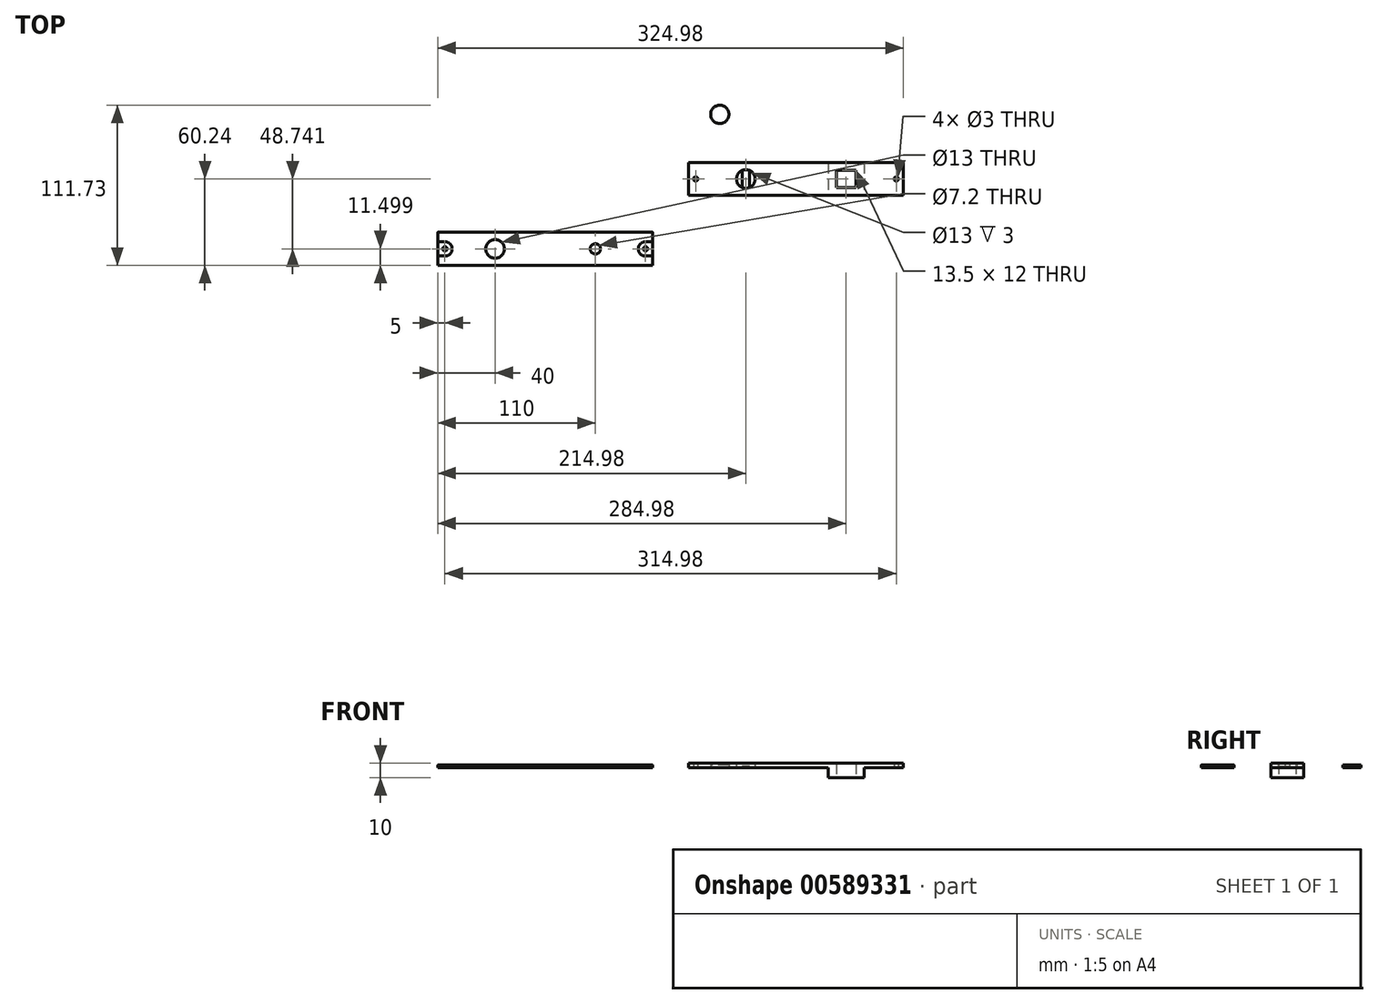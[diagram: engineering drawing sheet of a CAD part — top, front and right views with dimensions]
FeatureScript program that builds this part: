
annotation { "Feature Type Name" : "Feature", "Feature Type Description" : "" }
export const myFeature = defineFeature(function(context is Context, id is Id, definition is map)
    precondition{}
    {
        {
            var Q0;
            Q0=qCreatedBy(makeId("Top.planeOp"),FACE);
            var sketch = newSketch(context, id + "F0", { "sketchPlane" : qUnion([Q0])});
            skLineSegment(sketch, "E0.bottom", {"start": v(75, -11.5) * mm, "end": v(-75, -11.5) * mm});
            skLineSegment(sketch, "E0.top", {"start": v(75, 11.5) * mm, "end": v(-75, 11.5) * mm});
            skLineSegment(sketch, "E0.left", {"start": v(75, -11.5) * mm, "end": v(75, 11.5) * mm});
            skLineSegment(sketch, "E0.right", {"start": v(-75, -11.5) * mm, "end": v(-75, 11.5) * mm});
            skPoint(sketch, "E0.middle", {"position": v(0, 0) * mm});
            skCircle(sketch, "E1", {"center": v(-35, 0) * mm, "radius": 6.5 * mm});
            skLineSegment(sketch, "E2.bottom", {"start": v(-75, 11.5) * mm, "end": v(-65, 11.5) * mm, "construction": true});
            skLineSegment(sketch, "E2.top", {"start": v(-75, -11.5) * mm, "end": v(-65, -11.5) * mm, "construction": true});
            skLineSegment(sketch, "E2.left", {"start": v(-75, 11.5) * mm, "end": v(-75, -11.5) * mm, "construction": true});
            skLineSegment(sketch, "E2.right", {"start": v(-65, 11.5) * mm, "end": v(-65, -11.5) * mm, "construction": true});
            skLineSegment(sketch, "E3.bottom", {"start": v(75, -11.5) * mm, "end": v(65, -11.5) * mm, "construction": true});
            skLineSegment(sketch, "E3.top", {"start": v(75, 11.5) * mm, "end": v(65, 11.5) * mm, "construction": true});
            skLineSegment(sketch, "E3.left", {"start": v(75, -11.5) * mm, "end": v(75, 11.5) * mm, "construction": true});
            skLineSegment(sketch, "E3.right", {"start": v(65, -11.5) * mm, "end": v(65, 11.5) * mm, "construction": true});
            skLineSegment(sketch, "E4.bottom", {"start": v(41.75, -6) * mm, "end": v(28.25, -6) * mm});
            skLineSegment(sketch, "E4.top", {"start": v(41.75, 6) * mm, "end": v(28.25, 6) * mm});
            skLineSegment(sketch, "E4.left", {"start": v(41.75, -6) * mm, "end": v(41.75, 6) * mm});
            skLineSegment(sketch, "E4.right", {"start": v(28.25, -6) * mm, "end": v(28.25, 6) * mm});
            skPoint(sketch, "E4.middle", {"position": v(35, 0) * mm});
            skLineSegment(sketch, "E5.bottom", {"start": v(39, -6) * mm, "end": v(31, -6) * mm});
            skLineSegment(sketch, "E5.top", {"start": v(39, 6) * mm, "end": v(31, 6) * mm});
            skLineSegment(sketch, "E5.left", {"start": v(39, -6) * mm, "end": v(39, 6) * mm});
            skLineSegment(sketch, "E5.right", {"start": v(31, -6) * mm, "end": v(31, 6) * mm});
            skCircle(sketch, "E6", {"center": v(-70, 0) * mm, "radius": 1.5 * mm});
            skLineSegment(sketch, "E7.bottom", {"start": v(-65, 11.5) * mm, "end": v(-67, 11.5) * mm, "construction": true});
            skLineSegment(sketch, "E7.top", {"start": v(-65, -11.5) * mm, "end": v(-67, -11.5) * mm, "construction": true});
            skLineSegment(sketch, "E7.right", {"start": v(-67, 11.5) * mm, "end": v(-67, -11.5) * mm, "construction": true});
            skCircle(sketch, "E8", {"center": v(70, 0) * mm, "radius": 1.5 * mm});
            skLineSegment(sketch, "E9.bottom", {"start": v(-32.5, -6) * mm, "end": v(-37.5, -6) * mm, "construction": true});
            skLineSegment(sketch, "E9.top", {"start": v(-32.5, 6) * mm, "end": v(-37.5, 6) * mm, "construction": true});
            skLineSegment(sketch, "E9.left", {"start": v(-32.5, -6) * mm, "end": v(-32.5, 6) * mm});
            skLineSegment(sketch, "E9.right", {"start": v(-37.5, -6) * mm, "end": v(-37.5, 6) * mm});
            skSolve(sketch);
        }
        {
            var Q0;
            Q0=makeQuery(id+"F0.imprint","IMPRINT",FACE,{"disambiguationData":[TD([[makeQuery(id+"F0.imprint","IMPRINT",EDGE,{"derivedFrom":sQuery(id+"F0.wireOp",EDGE,"E0.bottom")}),-1.0]])]});
            var Q1;
            Q1=makeQuery(id+"F0.imprint","IMPRINT",FACE,{"disambiguationData":[TD([[makeQuery(id+"F0.imprint","IMPRINT",EDGE,{"derivedFrom":sQuery(id+"F0.wireOp",EDGE,"E5.bottom")}),-1.0]])]});
            var Q2;
            {var subQ0=sQuery(id+"F0.wireOp",EDGE,"E9.left");Q2=makeQuery(id+"F0.imprint","IMPRINT",FACE,{"disambiguationData":[TD([[makeQuery(id+"F0.imprint","IMPRINT",EDGE,{"derivedFrom":subQ0}),1.0]])]});}
            extrude(context, id + "F1", {"entities" : qUnion([Q0, Q1, Q2]), "depth" : 3 * mm});
        }
        {
            var Q0;
            Q0=qCreatedBy(makeId("Top.planeOp"),FACE);
            var sketch = newSketch(context, id + "F2", { "sketchPlane" : qUnion([Q0])});
            skLineSegment(sketch, "E10.bottom", {"start": v(-99.98, -60.24) * mm, "end": v(-249.98, -60.24) * mm});
            skLineSegment(sketch, "E10.top", {"start": v(-99.98, -37.24) * mm, "end": v(-249.98, -37.24) * mm});
            skLineSegment(sketch, "E10.left", {"start": v(-99.98, -60.24) * mm, "end": v(-99.98, -37.24) * mm});
            skLineSegment(sketch, "E10.right", {"start": v(-249.98, -60.24) * mm, "end": v(-249.98, -37.24) * mm});
            skPoint(sketch, "E10.middle", {"position": v(-174.98, -48.74) * mm});
            skCircle(sketch, "E11", {"center": v(-209.98, -48.74) * mm, "radius": 6.5 * mm});
            skLineSegment(sketch, "E12.bottom", {"start": v(-249.98, -37.24) * mm, "end": v(-239.98, -37.24) * mm, "construction": true});
            skLineSegment(sketch, "E12.top", {"start": v(-249.98, -60.24) * mm, "end": v(-239.98, -60.24) * mm, "construction": true});
            skLineSegment(sketch, "E12.left", {"start": v(-249.98, -37.24) * mm, "end": v(-249.98, -60.24) * mm, "construction": true});
            skLineSegment(sketch, "E12.right", {"start": v(-239.98, -37.24) * mm, "end": v(-239.98, -60.24) * mm, "construction": true});
            skLineSegment(sketch, "E13.bottom", {"start": v(-99.98, -60.24) * mm, "end": v(-109.98, -60.24) * mm, "construction": true});
            skLineSegment(sketch, "E13.top", {"start": v(-99.98, -37.24) * mm, "end": v(-109.98, -37.24) * mm, "construction": true});
            skLineSegment(sketch, "E13.left", {"start": v(-99.98, -60.24) * mm, "end": v(-99.98, -37.24) * mm, "construction": true});
            skLineSegment(sketch, "E13.right", {"start": v(-109.98, -60.24) * mm, "end": v(-109.98, -37.24) * mm, "construction": true});
            skLineSegment(sketch, "E14.bottom", {"start": v(-131.98, -55.74) * mm, "end": v(-147.98, -55.74) * mm, "construction": true});
            skLineSegment(sketch, "E14.top", {"start": v(-131.98, -41.74) * mm, "end": v(-147.98, -41.74) * mm, "construction": true});
            skLineSegment(sketch, "E14.left", {"start": v(-131.98, -55.74) * mm, "end": v(-131.98, -41.74) * mm, "construction": true});
            skLineSegment(sketch, "E14.right", {"start": v(-147.98, -55.74) * mm, "end": v(-147.98, -41.74) * mm, "construction": true});
            skPoint(sketch, "E14.middle", {"position": v(-139.98, -48.74) * mm});
            skLineSegment(sketch, "E15.bottom", {"start": v(-135.98, -55.74) * mm, "end": v(-143.98, -55.74) * mm});
            skLineSegment(sketch, "E15.top", {"start": v(-135.98, -41.74) * mm, "end": v(-143.98, -41.74) * mm});
            skLineSegment(sketch, "E15.left", {"start": v(-135.98, -55.74) * mm, "end": v(-135.98, -41.74) * mm, "construction": true});
            skLineSegment(sketch, "E15.right", {"start": v(-143.98, -55.74) * mm, "end": v(-143.98, -41.74) * mm, "construction": true});
            skCircle(sketch, "E16", {"center": v(-244.98, -48.74) * mm, "radius": 1.5 * mm});
            skCircle(sketch, "E17", {"center": v(-244.98, -55.24) * mm, "radius": 1.5 * mm, "construction": true});
            skCircle(sketch, "E18", {"center": v(-104.98, -48.74) * mm, "radius": 1.5 * mm});
            skCircle(sketch, "E19", {"center": v(-104.98, -55.24) * mm, "radius": 1.5 * mm, "construction": true});
            skCircle(sketch, "E20", {"center": v(-139.98, -48.74) * mm, "radius": 3.6 * mm});
            skLineSegment(sketch, "E21.bottom", {"start": v(-207.48, -54.74) * mm, "end": v(-212.48, -54.74) * mm, "construction": true});
            skLineSegment(sketch, "E21.top", {"start": v(-207.48, -42.74) * mm, "end": v(-212.48, -42.74) * mm, "construction": true});
            skLineSegment(sketch, "E21.left", {"start": v(-207.48, -54.74) * mm, "end": v(-207.48, -42.74) * mm});
            skLineSegment(sketch, "E21.right", {"start": v(-212.48, -54.74) * mm, "end": v(-212.48, -42.74) * mm});
            skSolve(sketch);
        }
        {
            var Q0;
            Q0=makeQuery(id+"F2.imprint","IMPRINT",FACE,{"disambiguationData":[TD([[makeQuery(id+"F2.imprint","IMPRINT",EDGE,{"derivedFrom":sQuery(id+"F2.wireOp",EDGE,"E10.bottom")}),-1.0]])]});
            extrude(context, id + "F3", {"entities" : qUnion([Q0]), "depth" : 2 * mm});
        }
        {
            var Q0;
            Q0=makeQuery(id+"F1.opExtrude","CAP_FACE",FACE,{"disambiguationData":[OSD([sQuery(id+"F0.wireOp",EDGE,"E0.bottom"),sQuery(id+"F0.wireOp",EDGE,"E0.top"),sQuery(id+"F0.wireOp",EDGE,"E0.left"),sQuery(id+"F0.wireOp",EDGE,"E0.right"),sQuery(id+"F0.wireOp",EDGE,"E1"),sQuery(id+"F0.wireOp",EDGE,"E4.bottom"),sQuery(id+"F0.wireOp",EDGE,"E4.top"),sQuery(id+"F0.wireOp",EDGE,"E4.left"),sQuery(id+"F0.wireOp",EDGE,"E4.right"),sQuery(id+"F0.wireOp",EDGE,"E5.left"),sQuery(id+"F0.wireOp",EDGE,"E5.right")])],"isStart":true});
            var sketch = newSketch(context, id + "F4", { "sketchPlane" : qUnion([Q0])});
            skPoint(sketch, "E22.0", {"position": v(35, 0) * mm});
            skLineSegment(sketch, "E23.bottom", {"start": v(47.5, -11.5) * mm, "end": v(22.5, -11.5) * mm});
            skLineSegment(sketch, "E23.top", {"start": v(47.5, 11.5) * mm, "end": v(22.5, 11.5) * mm});
            skLineSegment(sketch, "E23.left", {"start": v(47.5, -11.5) * mm, "end": v(47.5, 11.5) * mm});
            skLineSegment(sketch, "E23.right", {"start": v(22.5, -11.5) * mm, "end": v(22.5, 11.5) * mm});
            skLineSegment(sketch, "E24.bottom", {"start": v(41.75, -6) * mm, "end": v(28.25, -6) * mm});
            skLineSegment(sketch, "E24.top", {"start": v(41.75, 6) * mm, "end": v(28.25, 6) * mm});
            skLineSegment(sketch, "E24.left", {"start": v(41.75, -6) * mm, "end": v(41.75, 6) * mm});
            skLineSegment(sketch, "E24.right", {"start": v(28.25, -6) * mm, "end": v(28.25, 6) * mm});
            skLineSegment(sketch, "E25.bottom", {"start": v(39, -6) * mm, "end": v(31, -6) * mm});
            skLineSegment(sketch, "E25.top", {"start": v(39, 6) * mm, "end": v(31, 6) * mm});
            skLineSegment(sketch, "E25.left", {"start": v(39, -6) * mm, "end": v(39, 6) * mm});
            skLineSegment(sketch, "E25.right", {"start": v(31, -6) * mm, "end": v(31, 6) * mm});
            skSolve(sketch);
        }
        {
            var Q0;
            Q0=qSketchRegion(id+"F4",true);
            var Q1;
            Q1=makeQuery(id+"F0.imprint","IMPRINT",FACE,{"disambiguationData":[TD([[makeQuery(id+"F0.imprint","IMPRINT",EDGE,{"derivedFrom":sQuery(id+"F0.wireOp",EDGE,"E5.bottom")}),-1.0]])]});
            extrude(context, id + "F5", {"entities" : qUnion([Q0, Q1]), "operationType" : NewBodyOperationType.ADD, "depth" : 7 * mm});
        }
        {
            var Q0;
            Q0=makeQuery(id+"F1.opExtrude","CAP_FACE",FACE,{"disambiguationData":[OSD([sQuery(id+"F0.wireOp",EDGE,"E0.bottom"),sQuery(id+"F0.wireOp",EDGE,"E0.top"),sQuery(id+"F0.wireOp",EDGE,"E0.left"),sQuery(id+"F0.wireOp",EDGE,"E0.right"),sQuery(id+"F0.wireOp",EDGE,"E1"),sQuery(id+"F0.wireOp",EDGE,"E4.bottom"),sQuery(id+"F0.wireOp",EDGE,"E4.top"),sQuery(id+"F0.wireOp",EDGE,"E4.left"),sQuery(id+"F0.wireOp",EDGE,"E4.right"),sQuery(id+"F0.wireOp",EDGE,"E5.left"),sQuery(id+"F0.wireOp",EDGE,"E5.right")])],"isStart":false});
            var sketch = newSketch(context, id + "F6", { "sketchPlane" : qUnion([Q0])});
            skPoint(sketch, "E26.0", {"position": v(35, 0) * mm});
            skLineSegment(sketch, "E27.bottom", {"start": v(41.75, -6) * mm, "end": v(28.25, -6) * mm});
            skLineSegment(sketch, "E27.top", {"start": v(41.75, 6) * mm, "end": v(28.25, 6) * mm});
            skLineSegment(sketch, "E27.left", {"start": v(41.75, -6) * mm, "end": v(41.75, 6) * mm});
            skLineSegment(sketch, "E27.right", {"start": v(28.25, -6) * mm, "end": v(28.25, 6) * mm});
            skSolve(sketch);
        }
        {
            var Q0;
            Q0=qSketchRegion(id+"F6",true);
            extrude(context, id + "F7", {"entities" : qUnion([Q0]), "operationType" : NewBodyOperationType.REMOVE, "oppositeDirection" : true, "depth" : 9 * mm});
        }
        {
            var Q0;
            Q0=makeQuery(id+"F1.opExtrude","CAP_FACE",FACE,{"disambiguationData":[OSD([sQuery(id+"F0.wireOp",EDGE,"E0.bottom"),sQuery(id+"F0.wireOp",EDGE,"E0.top"),sQuery(id+"F0.wireOp",EDGE,"E0.left"),sQuery(id+"F0.wireOp",EDGE,"E0.right"),sQuery(id+"F0.wireOp",EDGE,"E1"),sQuery(id+"F0.wireOp",EDGE,"E4.bottom"),sQuery(id+"F0.wireOp",EDGE,"E4.top"),sQuery(id+"F0.wireOp",EDGE,"E4.left"),sQuery(id+"F0.wireOp",EDGE,"E4.right"),sQuery(id+"F0.wireOp",EDGE,"E5.left"),sQuery(id+"F0.wireOp",EDGE,"E5.right"),sQuery(id+"F0.wireOp",EDGE,"E6"),sQuery(id+"F0.wireOp",EDGE,"uwKOgWHx-wiQu-w8Me-ZzSO-K48oh4q2hqjQ"),sQuery(id+"F0.wireOp",EDGE,"E8"),sQuery(id+"F0.wireOp",EDGE,"GEiIiJwR-kFnx-osnd-0Qsu-TudxTzi2J8hG"),sQuery(id+"F0.wireOp",EDGE,"E9.left"),sQuery(id+"F0.wireOp",EDGE,"E9.right")])],"isStart":false});
            var sketch = newSketch(context, id + "F8", { "sketchPlane" : qUnion([Q0])});
            skPoint(sketch, "E28.0", {"position": v(-35, 0) * mm});
            skCircle(sketch, "E29", {"center": v(-35, 0) * mm, "radius": 6.5 * mm});
            skSolve(sketch);
        }
        {
            var Q0;
            Q0=qSketchRegion(id+"F8",true);
            extrude(context, id + "F9", {"entities" : qUnion([Q0]), "operationType" : NewBodyOperationType.REMOVE, "oppositeDirection" : true, "depth" : 2 * mm});
        }
        {
            var Q0;
            Q0=qCreatedBy(makeId("Top.planeOp"),FACE);
            var sketch = newSketch(context, id + "F10", { "sketchPlane" : qUnion([Q0])});
            skCircle(sketch, "E30", {"center": v(-53.16, 45.1) * mm, "radius": 6.4 * mm});
            skSolve(sketch);
        }
        {
            var Q0;
            Q0=makeQuery(id+"F10.imprint","IMPRINT",FACE,{"disambiguationData":[TD([[makeQuery(id+"F10.imprint","IMPRINT",EDGE,{"derivedFrom":sQuery(id+"F10.wireOp",EDGE,"E30")}),1.0]])]});
            extrude(context, id + "F11", {"entities" : qUnion([Q0]), "depth" : 2 * mm});
        }
        {
            var Q0;
            Q0=makeQuery(id+"F3.opExtrude","CAP_FACE",FACE,{"disambiguationData":[OSD([sQuery(id+"F2.wireOp",EDGE,"E10.bottom"),sQuery(id+"F2.wireOp",EDGE,"E10.top"),sQuery(id+"F2.wireOp",EDGE,"E10.left"),sQuery(id+"F2.wireOp",EDGE,"E10.right"),sQuery(id+"F2.wireOp",EDGE,"E11"),sQuery(id+"F2.wireOp",EDGE,"E16"),sQuery(id+"F2.wireOp",EDGE,"E17"),sQuery(id+"F2.wireOp",EDGE,"E18"),sQuery(id+"F2.wireOp",EDGE,"E19"),sQuery(id+"F2.wireOp",EDGE,"E20")])],"isStart":false});
            var sketch = newSketch(context, id + "F12", { "sketchPlane" : qUnion([Q0])});
            skCircle(sketch, "E31", {"center": v(-244.98, -48.74) * mm, "radius": 5 * mm});
            skCircle(sketch, "E32", {"center": v(-104.98, -48.74) * mm, "radius": 5 * mm});
            skLineSegment(sketch, "E33.bottom", {"start": v(-244.98, -53.74) * mm, "end": v(-252.48, -53.74) * mm});
            skLineSegment(sketch, "E33.top", {"start": v(-244.98, -43.74) * mm, "end": v(-252.48, -43.74) * mm});
            skLineSegment(sketch, "E33.right", {"start": v(-252.48, -53.74) * mm, "end": v(-252.48, -43.74) * mm});
            skLineSegment(sketch, "E34.bottom", {"start": v(-97.48, -53.74) * mm, "end": v(-104.98, -53.74) * mm});
            skLineSegment(sketch, "E34.top", {"start": v(-97.48, -43.74) * mm, "end": v(-104.98, -43.74) * mm});
            skLineSegment(sketch, "E34.left", {"start": v(-97.48, -53.74) * mm, "end": v(-97.48, -43.74) * mm});
            skSolve(sketch);
        }
        {
            var Q0;
            Q0=qSketchRegion(id+"F12",true);
            extrude(context, id + "F13", {"entities" : qUnion([Q0]), "operationType" : NewBodyOperationType.REMOVE, "oppositeDirection" : true, "depth" : 1 * mm});
        }
        {
            var Q0;
            Q0=makeQuery(id+"F3.opExtrude","CAP_EDGE",EDGE,{"disambiguationData":[OSD([sQuery(id+"F2.wireOp",EDGE,"E10.top")])],"isStart":false});
            var Q1;
            {var subQ0=sQuery(id+"F2.wireOp",EDGE,"E10.right");var subQ1=sQuery(id+"F2.wireOp",EDGE,"E10.top");Q1=makeQuery(id+"F13.boolean.opBoolean","SPLIT",EDGE,{"disambiguationData":[TD([makeQuery(id+"F3.opExtrude","SWEPT_FACE",FACE,{"disambiguationData":[OSD([subQ1])]})])],"derivedFrom":makeQuery(id+"F3.opExtrude","CAP_EDGE",EDGE,{"disambiguationData":[OSD([subQ0])],"isStart":false})});}
            var Q2;
            Q2=makeQuery(id+"F13.boolean.opBoolean","COPY",EDGE,{"derivedFrom":makeQuery(id+"F13.opExtrude","CAP_EDGE",EDGE,{"disambiguationData":[OSD([sQuery(id+"F12.wireOp",EDGE,"E33.top")])],"isStart":true})});
            var Q3;
            {var subQ0=sQuery(id+"F2.wireOp",EDGE,"E10.bottom");var subQ1=sQuery(id+"F2.wireOp",EDGE,"E10.right");Q3=makeQuery(id+"F13.boolean.opBoolean","SPLIT",EDGE,{"disambiguationData":[TD([makeQuery(id+"F3.opExtrude","SWEPT_FACE",FACE,{"disambiguationData":[OSD([subQ0])]})])],"derivedFrom":makeQuery(id+"F3.opExtrude","CAP_EDGE",EDGE,{"disambiguationData":[OSD([subQ1])],"isStart":false})});}
            var Q4;
            Q4=makeQuery(id+"F3.opExtrude","CAP_EDGE",EDGE,{"disambiguationData":[OSD([sQuery(id+"F2.wireOp",EDGE,"E10.bottom")])],"isStart":false});
            var Q5;
            {var subQ0=sQuery(id+"F2.wireOp",EDGE,"E10.bottom");var subQ1=sQuery(id+"F2.wireOp",EDGE,"E10.left");Q5=makeQuery(id+"F13.boolean.opBoolean","SPLIT",EDGE,{"disambiguationData":[TD([makeQuery(id+"F3.opExtrude","SWEPT_FACE",FACE,{"disambiguationData":[OSD([subQ0])]})])],"derivedFrom":makeQuery(id+"F3.opExtrude","CAP_EDGE",EDGE,{"disambiguationData":[OSD([subQ1])],"isStart":false})});}
            var Q6;
            Q6=makeQuery(id+"F13.boolean.opBoolean","COPY",EDGE,{"derivedFrom":makeQuery(id+"F13.opExtrude","CAP_EDGE",EDGE,{"disambiguationData":[OSD([sQuery(id+"F12.wireOp",EDGE,"E34.bottom")])],"isStart":true})});
            var Q7;
            {var subQ0=sQuery(id+"F2.wireOp",EDGE,"E10.left");var subQ1=sQuery(id+"F2.wireOp",EDGE,"E10.top");Q7=makeQuery(id+"F13.boolean.opBoolean","SPLIT",EDGE,{"disambiguationData":[TD([makeQuery(id+"F3.opExtrude","SWEPT_FACE",FACE,{"disambiguationData":[OSD([subQ1])]})])],"derivedFrom":makeQuery(id+"F3.opExtrude","CAP_EDGE",EDGE,{"disambiguationData":[OSD([subQ0])],"isStart":false})});}
            fillet(context, id + "F14", {"entities" : qUnion([Q0, Q1, Q2, Q3, Q4, Q5, Q6, Q7]), "radius" : 0.5 * mm, "tangentPropagation" : true, "allowEdgeOverflow" : false});
        }
    });
